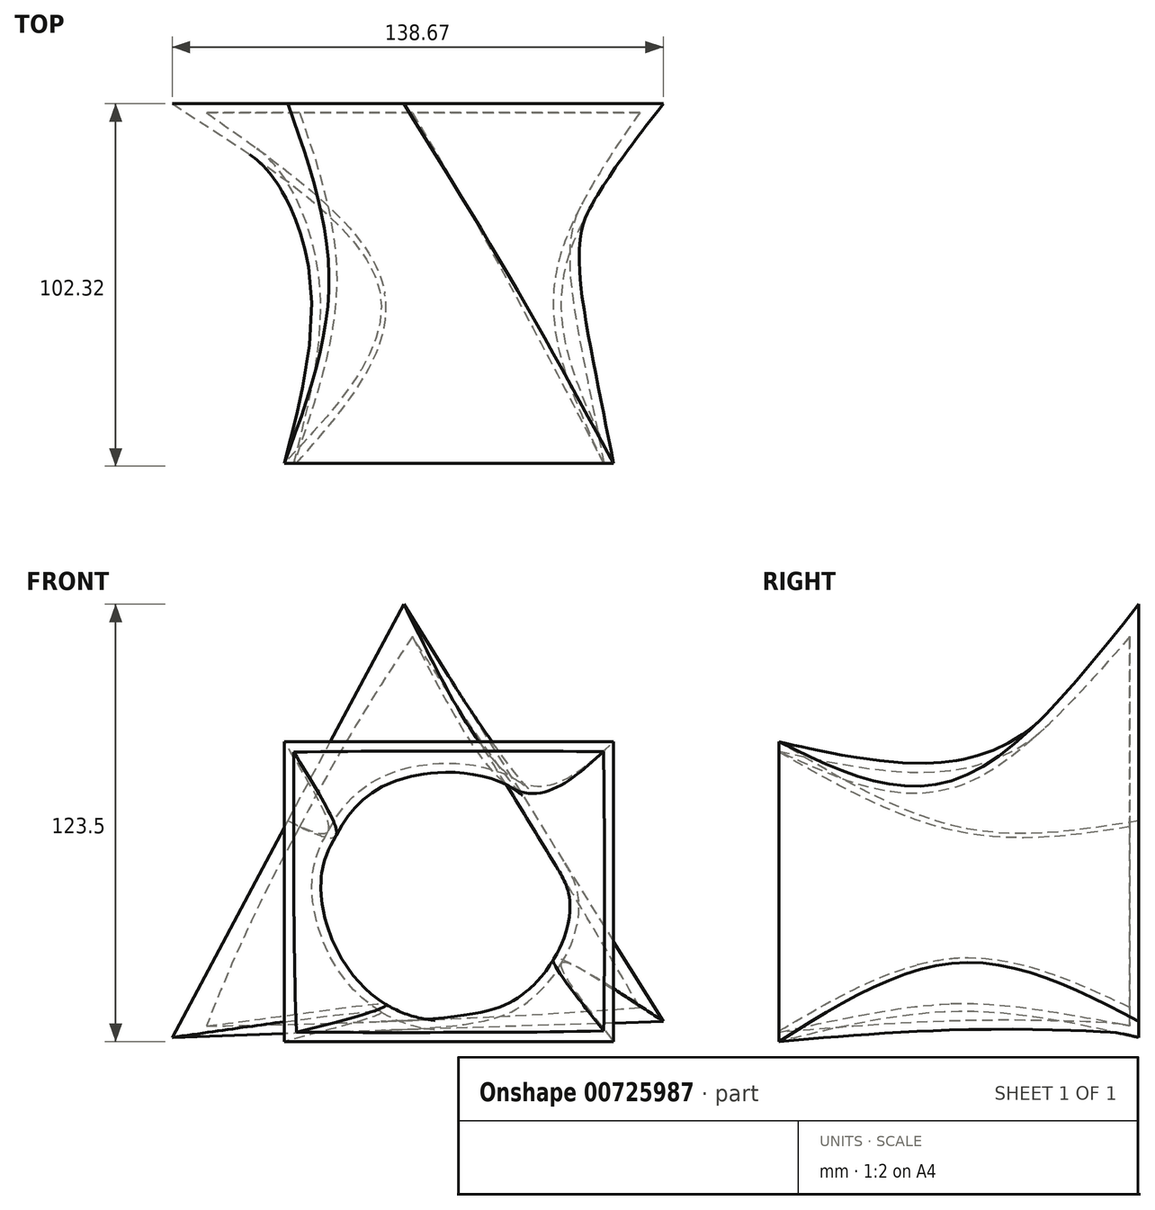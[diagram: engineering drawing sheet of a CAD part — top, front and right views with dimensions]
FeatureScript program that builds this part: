
annotation { "Feature Type Name" : "Feature", "Feature Type Description" : "" }
export const myFeature = defineFeature(function(context is Context, id is Id, definition is map)
    precondition{}
    {
        {
            var Q0;
            Q0=qCreatedBy(makeId("Front.planeOp"),FACE);
            cPlane(context, id + "F0", {"entities" : qUnion([Q0]), "cplaneType" : CPlaneType.OFFSET, "offset" : 50.8 * mm, "width" : 152.4 * mm, "height" : 152.4 * mm});
        }
        {
            var Q0;
            Q0=qCreatedBy(makeId("Front.planeOp"),FACE);
            cPlane(context, id + "F1", {"entities" : qUnion([Q0]), "cplaneType" : CPlaneType.OFFSET, "offset" : 50.8 * mm, "oppositeDirection" : true, "width" : 152.4 * mm, "height" : 152.4 * mm});
        }
        {
            var Q0;
            Q0=qCreatedBy(id+"F0.planeOp",FACE);
            var sketch = newSketch(context, id + "F2", { "sketchPlane" : qUnion([Q0])});
            skLineSegment(sketch, "E0.bottom", {"start": v(-45.58, 43.25) * mm, "end": v(47.44, 43.25) * mm});
            skLineSegment(sketch, "E0.top", {"start": v(-45.58, -41.4) * mm, "end": v(47.44, -41.4) * mm});
            skLineSegment(sketch, "E0.left", {"start": v(-45.58, 43.25) * mm, "end": v(-45.58, -41.4) * mm});
            skLineSegment(sketch, "E0.right", {"start": v(47.44, 43.25) * mm, "end": v(47.44, -41.4) * mm});
            skSolve(sketch);
        }
        {
            var Q0;
            Q0=qCreatedBy(makeId("Front.planeOp"),FACE);
            var sketch = newSketch(context, id + "F3", { "sketchPlane" : qUnion([Q0])});
            skCircle(sketch, "E1", {"center": v(0, 0) * mm, "radius": 38.1 * mm});
            skSolve(sketch);
        }
        {
            var Q0;
            Q0=qCreatedBy(id+"F1.planeOp",FACE);
            var sketch = newSketch(context, id + "F4", { "sketchPlane" : qUnion([Q0])});
            skLineSegment(sketch, "E2.0", {"start": v(61.44, -35.72) * mm, "end": v(-77.23, -40.25) * mm});
            skLineSegment(sketch, "E2.1", {"start": v(-77.23, -40.25) * mm, "end": v(-11.82, 82.1) * mm});
            skLineSegment(sketch, "E2.2", {"start": v(-11.82, 82.1) * mm, "end": v(61.44, -35.72) * mm});
            skPoint(sketch, "E2.0.midPoint", {"position": v(-9.53, 27.63) * mm});
            skSolve(sketch);
        }
        {
            var Q0;
            Q0=makeQuery(id+"F4.imprint","IMPRINT",FACE,{"disambiguationData":[TD([[makeQuery(id+"F4.imprint","IMPRINT",EDGE,{"derivedFrom":sQuery(id+"F4.wireOp",EDGE,"E2.0")}),-1.0]])]});
            var Q1;
            Q1=makeQuery(id+"F3.imprint","IMPRINT",FACE,{"disambiguationData":[TD([[makeQuery(id+"F3.imprint","IMPRINT",EDGE,{"derivedFrom":sQuery(id+"F3.wireOp",EDGE,"E1")}),1.0]])]});
            var Q2;
            Q2=makeQuery(id+"F2.imprint","IMPRINT",FACE,{"disambiguationData":[TD([[makeQuery(id+"F2.imprint","IMPRINT",EDGE,{"derivedFrom":sQuery(id+"F2.wireOp",EDGE,"E0.bottom")}),-1.0]])]});
            loft(context, id + "F5", {"sheetProfilesArray" : [{ "sheetProfileEntities" : qUnion([Q0]) }, { "sheetProfileEntities" : qUnion([Q1]) }, { "sheetProfileEntities" : qUnion([Q2]) }]});
        }
        {
            var Q0;
            Q0=makeQuery(id+"F5.opLoft","CAP_FACE",FACE,{"disambiguationData":[OSD([makeQuery(id+"F2.imprint","IMPRINT",FACE,{"disambiguationData":[TD([[makeQuery(id+"F2.imprint","IMPRINT",EDGE,{"derivedFrom":sQuery(id+"F2.wireOp",EDGE,"E0.bottom")}),-1.0]])]})])],"isStart":true});
            shell(context, id + "F6", {"entities" : qUnion([Q0]), "thickness" : 2.54 * mm});
        }
    });
